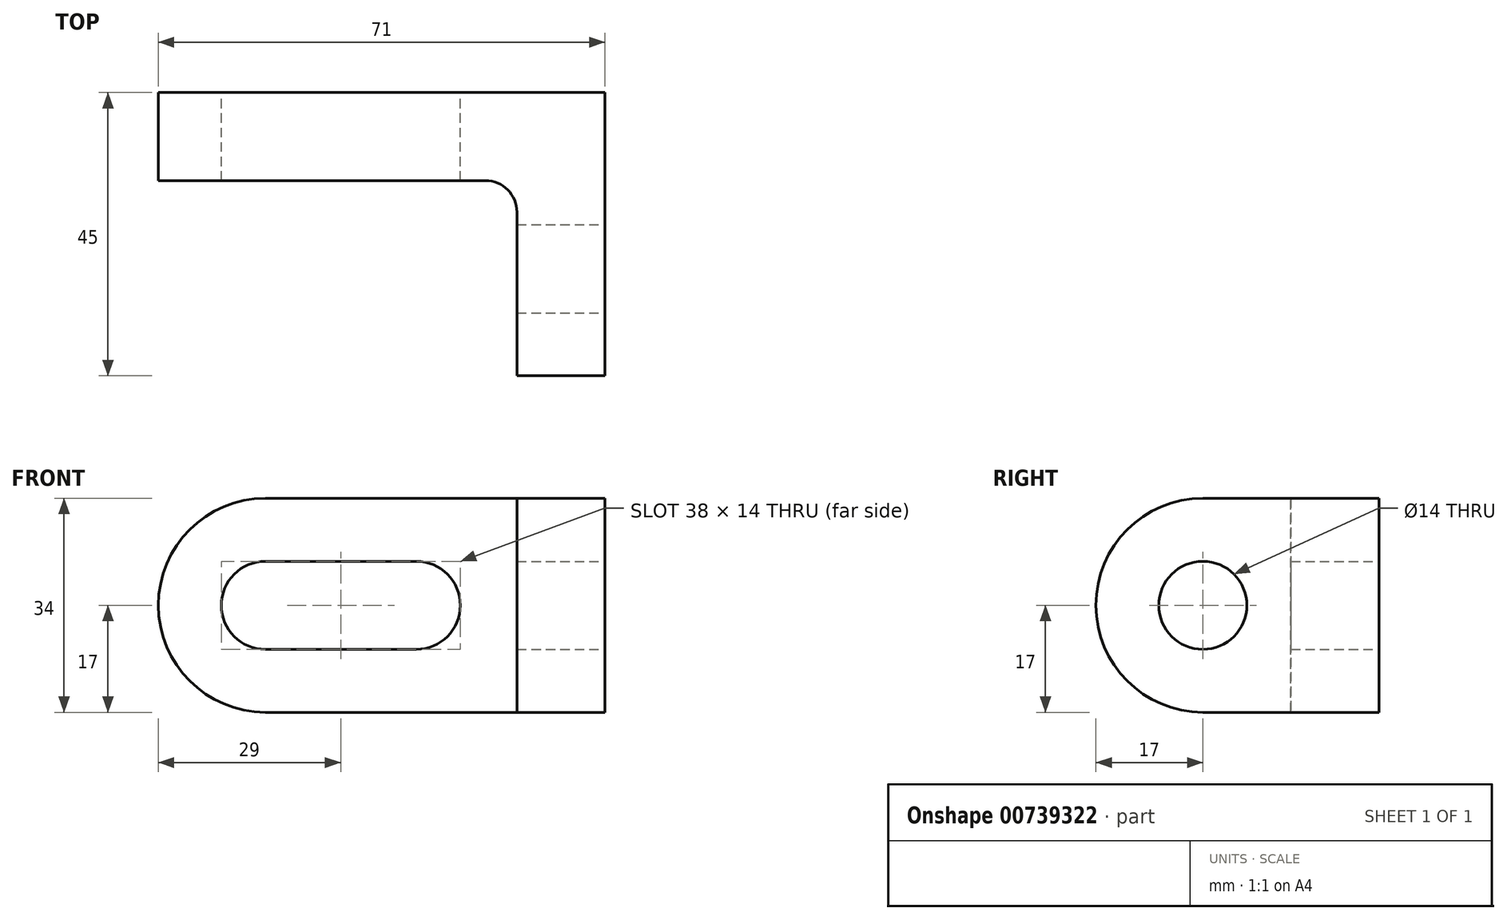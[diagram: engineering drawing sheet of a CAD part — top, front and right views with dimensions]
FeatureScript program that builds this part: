
annotation { "Feature Type Name" : "Feature", "Feature Type Description" : "" }
export const myFeature = defineFeature(function(context is Context, id is Id, definition is map)
    precondition{}
    {
        {
            var Q0;
            Q0=qCreatedBy(makeId("Front.planeOp"),FACE);
            var sketch = newSketch(context, id + "F0", { "sketchPlane" : qUnion([Q0])});
            skLineSegment(sketch, "E0.bottom", {"start": v(-27, 17) * mm, "end": v(27, 17) * mm});
            skLineSegment(sketch, "E0.top", {"start": v(-27, -17) * mm, "end": v(27, -17) * mm});
            skLineSegment(sketch, "E0.right", {"start": v(27, 17) * mm, "end": v(27, -17) * mm});
            skPoint(sketch, "E0.middle", {"position": v(0, 0) * mm});
            skArc(sketch, "E1", {"start": v(-27, 17) * mm, "mid": v(-44, 0) * mm, "end": v(-27, -17) * mm});
            skLineSegment(sketch, "E2.bottom", {"start": v(-27, -7) * mm, "end": v(-3, -7) * mm});
            skLineSegment(sketch, "E2.top", {"start": v(-27, 7) * mm, "end": v(-3, 7) * mm});
            skArc(sketch, "E3", {"start": v(-27, 7) * mm, "mid": v(-34, 0) * mm, "end": v(-27, -7) * mm});
            skArc(sketch, "E4", {"start": v(-3, -7) * mm, "mid": v(4, 0) * mm, "end": v(-3, 7) * mm});
            skSolve(sketch);
        }
        {
            var Q0;
            Q0 = qSketchRegion(id + "F0", true);
            extrude(context, id + "F1", {"entities" : qUnion([Q0]), "depth" : 14 * mm, "offsetDistance" : 25 * mm});
        }
        {
            var Q0;
            Q0=makeQuery(id+"F1.opExtrude","SWEPT_FACE",FACE,{"disambiguationData":[OSD([sQuery(id+"F0.wireOp",EDGE,"E0.right")])]});
            var sketch = newSketch(context, id + "F2", { "sketchPlane" : qUnion([Q0])});
            skLineSegment(sketch, "E5.bottom", {"start": v(0, -17) * mm, "end": v(-28, -17) * mm});
            skLineSegment(sketch, "E5.top", {"start": v(0, 17) * mm, "end": v(-28, 17) * mm});
            skLineSegment(sketch, "E5.left", {"start": v(0, -17) * mm, "end": v(0, 17) * mm});
            skArc(sketch, "E6", {"start": v(-28, 17) * mm, "mid": v(-45, 0) * mm, "end": v(-28, -17) * mm});
            skCircle(sketch, "E7", {"center": v(-28, 0) * mm, "radius": 7 * mm});
            skSolve(sketch);
        }
        {
            var Q0;
            Q0 = qSketchRegion(id + "F2", true);
            extrude(context, id + "F3", {"entities" : qUnion([Q0]), "operationType" : NewBodyOperationType.ADD, "oppositeDirection" : true, "depth" : 14 * mm, "offsetDistance" : 25 * mm});
        }
        {
            var Q0;
            Q0=makeQuery(id+"F3.boolean.opBoolean","INTERSECT",EDGE,{"derivedFrom":[makeQuery(id+"F1.opExtrude","CAP_FACE",FACE,{"disambiguationData":[OSD([sQuery(id+"F0.wireOp",EDGE,"E0.bottom"),sQuery(id+"F0.wireOp",EDGE,"E0.top"),sQuery(id+"F0.wireOp",EDGE,"E0.right"),sQuery(id+"F0.wireOp",EDGE,"E1"),sQuery(id+"F0.wireOp",EDGE,"E2.bottom"),sQuery(id+"F0.wireOp",EDGE,"E2.top"),sQuery(id+"F0.wireOp",EDGE,"E3"),sQuery(id+"F0.wireOp",EDGE,"E4")])],"isStart":false}),makeQuery(id+"F3.opExtrude","CAP_FACE",FACE,{"disambiguationData":[OSD([sQuery(id+"F2.wireOp",EDGE,"E5.bottom"),sQuery(id+"F2.wireOp",EDGE,"E5.top"),sQuery(id+"F2.wireOp",EDGE,"E5.left"),sQuery(id+"F2.wireOp",EDGE,"E6"),sQuery(id+"F2.wireOp",EDGE,"E7")])],"isStart":false})]});
            fillet(context, id + "F4", {"entities" : qUnion([Q0]), "radius" : 5 * mm, "tangentPropagation" : true, "allowEdgeOverflow" : false});
        }
    });
